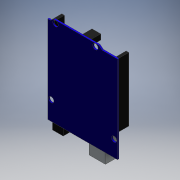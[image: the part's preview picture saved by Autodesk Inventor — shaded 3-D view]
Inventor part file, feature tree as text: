
AUTODESK INVENTOR PART (.ipt)
format: ipt  version: 2016 (Build 200138000, 138)  size: 186,368 bytes
history: native  units: mm
features: sketch x7, extrude x6, other x1
ambient origin geometry x8: Origin, YZ Plane, XZ Plane, XY Plane, X Axis, Y Axis, Z Axis, Center Point
bodies: Body1 (feature_tree)
feature tree (14):
  other  "Sólido1"
  extrude  "Extrusión1"  Depth=8.45mm TaperAngle=0.0deg
  extrude  "Extrusión2"  Depth=10.0mm TaperAngle=0.0deg
  extrude  "Extrusión3"  Depth=12.0mm TaperAngle=0.0deg
  extrude  "Extrusión4"  [1 undecoded]
  extrude  "Extrusión5"  [1 undecoded]
  extrude  "Extrusión6"  [1 undecoded]
  sketch  "Boceto7"
  sketch  "Boceto1"  dims[d25=1.0mm d26=0.0mm d39=8.45mm d40=0.0mm]
  sketch  "Boceto2"  dims[d45=8.0mm d46=0.0mm d51=10.0mm d52=0.0mm]
  sketch  "Boceto3"  dims[d57=10.0mm d58=0.0mm d60=12.0mm d61=0.0mm]
  sketch  "Boceto4"
  sketch  "Boceto5"
  sketch  "Boceto6"
note: 3 required parameter values undecoded (feature->parameter linkage not recoverable at this tier; creation-order binding heuristic only, values carry confidence <= 0.55)
